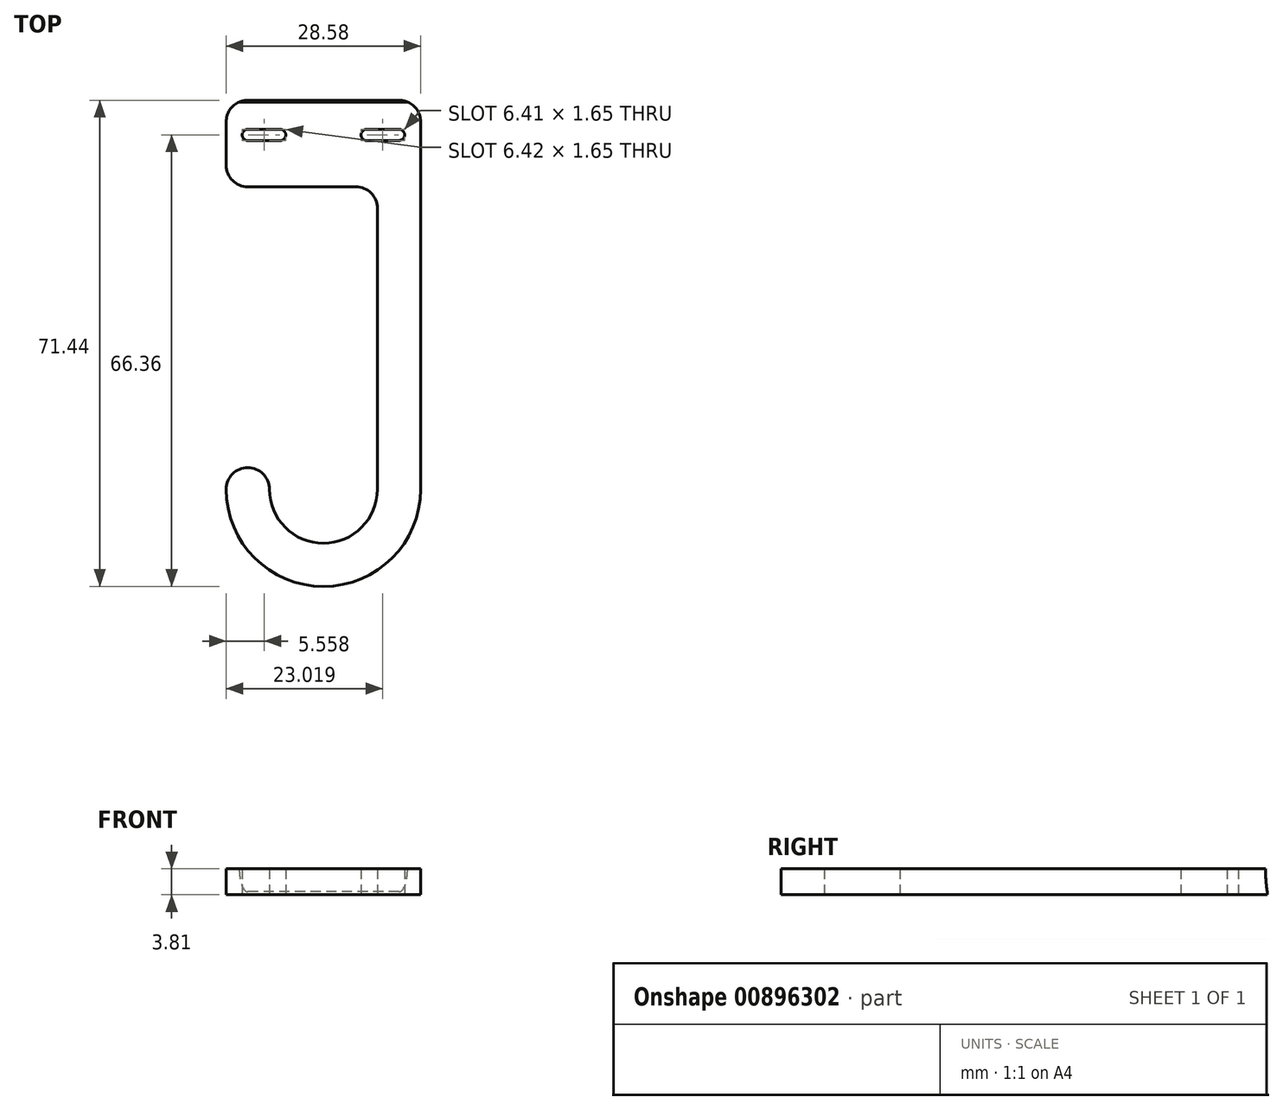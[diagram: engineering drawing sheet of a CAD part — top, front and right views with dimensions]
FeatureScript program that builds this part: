
annotation { "Feature Type Name" : "Feature", "Feature Type Description" : "" }
export const myFeature = defineFeature(function(context is Context, id is Id, definition is map)
    precondition{}
    {
        {
            var Q0;
            Q0=qCreatedBy(makeId("Top.planeOp"),FACE);
            var sketch = newSketch(context, id + "F0", { "sketchPlane" : qUnion([Q0])});
            skArc(sketch, "E0", {"start": v(-7.94, 0) * mm, "mid": v(0, -7.94) * mm, "end": v(7.94, 0) * mm});
            skArc(sketch, "E1", {"start": v(-14.29, 0) * mm, "mid": v(0, -14.29) * mm, "end": v(14.29, 0) * mm});
            skLineSegment(sketch, "E2", {"start": v(-11.11, 57.15) * mm, "end": v(11.11, 57.15) * mm});
            skLineSegment(sketch, "E3", {"start": v(14.29, 53.98) * mm, "end": v(14.29, 0) * mm});
            skLineSegment(sketch, "E4.0", {"start": v(-11.11, 44.45) * mm, "end": v(4.76, 44.45) * mm});
            skLineSegment(sketch, "E5.0", {"start": v(7.94, 41.28) * mm, "end": v(7.94, 0) * mm});
            skLineSegment(sketch, "E6.0", {"start": v(-11.11, 3.17) * mm, "end": v(-11.11, 3.17) * mm});
            skLineSegment(sketch, "E7.trimOffspring", {"start": v(-14.29, 47.62) * mm, "end": v(-14.29, 53.98) * mm});
            skPoint(sketch, "E8.start.orphan", {"position": v(-14.29, 0) * mm});
            skPoint(sketch, "E9.visualSharp", {"position": v(-14.29, 44.45) * mm});
            skArc(sketch, "E9.filletArc", {"start": v(-14.29, 47.62) * mm, "mid": v(-13.36, 45.38) * mm, "end": v(-11.11, 44.45) * mm});
            skPoint(sketch, "E10.visualSharp", {"position": v(-14.29, 57.15) * mm});
            skArc(sketch, "E10.filletArc", {"start": v(-11.11, 57.15) * mm, "mid": v(-13.36, 56.22) * mm, "end": v(-14.29, 53.98) * mm});
            skPoint(sketch, "E11.visualSharp", {"position": v(14.29, 57.15) * mm});
            skArc(sketch, "E11.filletArc", {"start": v(14.29, 53.98) * mm, "mid": v(13.36, 56.22) * mm, "end": v(11.11, 57.15) * mm});
            skPoint(sketch, "E12.visualSharp", {"position": v(7.94, 44.45) * mm});
            skArc(sketch, "E12.filletArc", {"start": v(7.94, 41.28) * mm, "mid": v(7, 43.52) * mm, "end": v(4.76, 44.45) * mm});
            skPoint(sketch, "E13.visualSharp", {"position": v(-13.93, 3.17) * mm});
            skArc(sketch, "E13.filletArc", {"start": v(-11.11, 3.17) * mm, "mid": v(-13.36, 2.25) * mm, "end": v(-14.29, 0) * mm});
            skPoint(sketch, "E14.visualSharp", {"position": v(-7.27, 3.17) * mm});
            skArc(sketch, "E14.filletArc", {"start": v(-7.94, 0) * mm, "mid": v(-8.87, 2.25) * mm, "end": v(-11.11, 3.17) * mm});
            skArc(sketch, "E15", {"start": v(-11.11, 52.9) * mm, "mid": v(-11.94, 52.07) * mm, "end": v(-11.11, 51.24) * mm});
            skArc(sketch, "E16", {"start": v(11.11, 51.25) * mm, "mid": v(11.93, 52.07) * mm, "end": v(11.11, 52.9) * mm});
            skArc(sketch, "E17", {"start": v(-6.35, 51.24) * mm, "mid": v(-5.52, 52.07) * mm, "end": v(-6.35, 52.9) * mm});
            skArc(sketch, "E18", {"start": v(6.35, 52.9) * mm, "mid": v(5.52, 52.07) * mm, "end": v(6.35, 51.24) * mm});
            skLineSegment(sketch, "E19", {"start": v(-11.11, 52.9) * mm, "end": v(-6.35, 52.9) * mm});
            skLineSegment(sketch, "E20", {"start": v(-11.11, 51.24) * mm, "end": v(-6.35, 51.24) * mm});
            skLineSegment(sketch, "E21", {"start": v(6.35, 52.9) * mm, "end": v(11.11, 52.9) * mm});
            skLineSegment(sketch, "E22", {"start": v(6.35, 51.24) * mm, "end": v(11.11, 51.25) * mm});
            skSolve(sketch);
        }
        {
            var Q0;
            Q0=makeQuery(id+"F0.imprint","IMPRINT",FACE,{"disambiguationData":[TD([[makeQuery(id+"F0.imprint","IMPRINT",EDGE,{"derivedFrom":sQuery(id+"F0.wireOp",EDGE,"E0")}),-1.0]])]});
            extrude(context, id + "F1", {"entities" : qUnion([Q0]), "flatOperationType" : FlatOperationType.REMOVE, "depth" : 3.8 * mm, "offsetDistance" : 25.4 * mm, "domain" : OperationDomain.MODEL});
        }
        {
            var Q0;
            Q0=makeQuery(id+"F1.opExtrude","SWEPT_FACE",FACE,{"disambiguationData":[OSD([sQuery(id+"F0.wireOp",EDGE,"E7.trimOffspring")])]});
            var sketch = newSketch(context, id + "F2", { "sketchPlane" : qUnion([Q0])});
            skLineSegment(sketch, "E23.0", {"start": v(-57.15, 3.81) * mm, "end": v(-57.15, 0) * mm});
            skPoint(sketch, "E24.0", {"position": v(-57.15, 3.81) * mm});
            skPoint(sketch, "E25.0", {"position": v(14.29, 3.81) * mm});
            skPoint(sketch, "E26.0", {"position": v(14.29, 0) * mm});
            skPoint(sketch, "E27.0", {"position": v(-57.15, 0) * mm});
            skCircle(sketch, "E28", {"center": v(79.12, 3.81) * mm, "radius": 22.23 * mm});
            skLineSegment(sketch, "E29.0", {"start": v(-79.12, 7.62) * mm, "end": v(-79.12, 0) * mm});
            skCircle(sketch, "E30", {"center": v(-79.12, 3.81) * mm, "radius": 22.23 * mm});
            skSolve(sketch);
        }
        {
            var Q0;
            Q0 = qSketchRegion(id + "F2", true);
            extrude(context, id + "F3", {"entities" : qUnion([Q0]), "operationType" : NewBodyOperationType.REMOVE, "endBound" : BoundingType.THROUGH_ALL, "depth" : 50.8 * mm, "offsetDistance" : 25.4 * mm});
        }
        {
            var Q0;
            Q0 = qSketchRegion(id + "F2", true);
            extrude(context, id + "F4", {"entities" : qUnion([Q0]), "operationType" : NewBodyOperationType.REMOVE, "endBound" : BoundingType.THROUGH_ALL, "oppositeDirection" : true, "depth" : 50.8 * mm, "offsetDistance" : 25.4 * mm});
        }
    });
